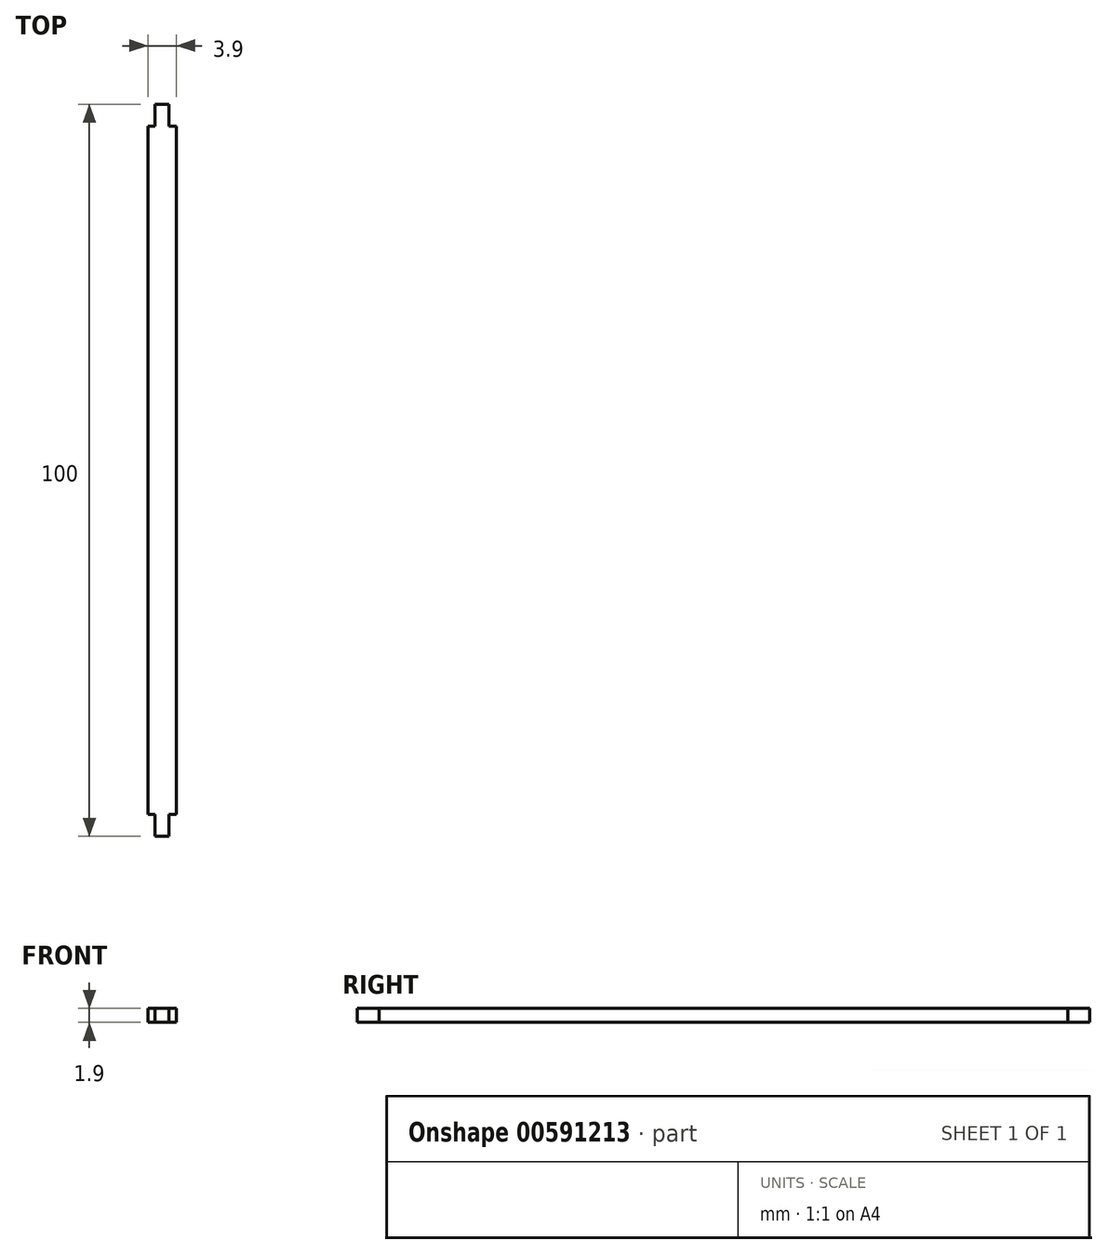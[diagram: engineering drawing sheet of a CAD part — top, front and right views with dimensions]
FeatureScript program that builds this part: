
annotation { "Feature Type Name" : "Feature", "Feature Type Description" : "" }
export const myFeature = defineFeature(function(context is Context, id is Id, definition is map)
    precondition{}
    {
        {
            var Q0;
            Q0=qCreatedBy(makeId("Top.planeOp"),FACE);
            var sketch = newSketch(context, id + "F0", { "sketchPlane" : qUnion([Q0])});
            skLineSegment(sketch, "E0.bottom", {"start": v(-32.6, 47.63) * mm, "end": v(-30.7, 47.63) * mm});
            skLineSegment(sketch, "E0.top", {"start": v(-32.6, -52.37) * mm, "end": v(-30.7, -52.37) * mm});
            skLineSegment(sketch, "E0.left", {"start": v(-32.6, 47.63) * mm, "end": v(-32.6, 44.63) * mm});
            skLineSegment(sketch, "E0.right", {"start": v(-30.7, 47.63) * mm, "end": v(-30.7, 44.63) * mm});
            skLineSegment(sketch, "E1.bottom", {"start": v(-33.6, 44.63) * mm, "end": v(-32.6, 44.63) * mm});
            skLineSegment(sketch, "E1.top", {"start": v(-33.6, -49.37) * mm, "end": v(-32.6, -49.37) * mm});
            skLineSegment(sketch, "E1.left", {"start": v(-33.6, 44.63) * mm, "end": v(-33.6, -49.37) * mm});
            skLineSegment(sketch, "E1.right", {"start": v(-29.7, 44.63) * mm, "end": v(-29.7, -49.37) * mm});
            skLineSegment(sketch, "E2.trimOffspring", {"start": v(-30.7, -49.37) * mm, "end": v(-30.7, -52.37) * mm});
            skLineSegment(sketch, "E3.trimOffspring", {"start": v(-30.7, 44.63) * mm, "end": v(-29.7, 44.63) * mm});
            skLineSegment(sketch, "E4.trimOffspring", {"start": v(-32.6, -49.37) * mm, "end": v(-32.6, -52.37) * mm});
            skLineSegment(sketch, "E5.trimOffspring", {"start": v(-30.7, -49.37) * mm, "end": v(-29.7, -49.37) * mm});
            skSolve(sketch);
        }
        {
            var Q0;
            Q0=makeQuery(id+"F0.imprint","IMPRINT",FACE,{"disambiguationData":[TD([[makeQuery(id+"F0.imprint","IMPRINT",EDGE,{"derivedFrom":sQuery(id+"F0.wireOp",EDGE,"E0.bottom")}),-1.0]])]});
            extrude(context, id + "F1", {"entities" : qUnion([Q0]), "depth" : 1.9 * mm, "offsetDistance" : 25 * mm});
        }
    });
